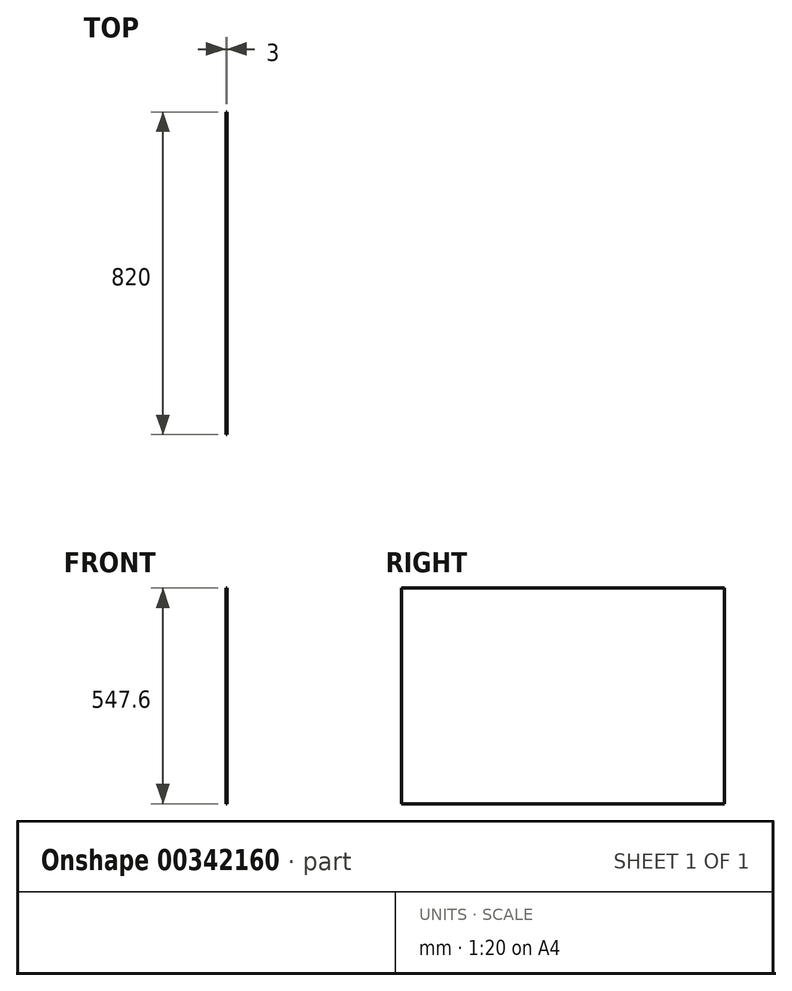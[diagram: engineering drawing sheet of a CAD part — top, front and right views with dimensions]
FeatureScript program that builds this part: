
annotation { "Feature Type Name" : "Feature", "Feature Type Description" : "" }
export const myFeature = defineFeature(function(context is Context, id is Id, definition is map)
    precondition{}
    {
        {
            var Q0;
            Q0=qCreatedBy(makeId("Front.planeOp"),FACE);
            var sketch = newSketch(context, id + "F0", { "sketchPlane" : qUnion([Q0])});
            skLineSegment(sketch, "E0", {"start": v(-856.22, 350.08) * mm, "end": v(-856.22, -197.52) * mm});
            skLineSegment(sketch, "E1", {"start": v(-856.22, -197.52) * mm, "end": v(-291.22, -297.92) * mm});
            skLineSegment(sketch, "E2", {"start": v(1143.78, -552.92) * mm, "end": v(1143.78, -5.32) * mm});
            skLineSegment(sketch, "E3", {"start": v(1143.78, -5.32) * mm, "end": v(-856.22, 350.08) * mm});
            skLineSegment(sketch, "E4.bottom", {"start": v(-856.22, 350.08) * mm, "end": v(-859.22, 350.08) * mm});
            skLineSegment(sketch, "E4.top", {"start": v(-856.22, -197.52) * mm, "end": v(-859.22, -197.52) * mm});
            skLineSegment(sketch, "E4.right", {"start": v(-859.22, 350.08) * mm, "end": v(-859.22, -197.52) * mm});
            skLineSegment(sketch, "E5", {"start": v(-291.22, -297.92) * mm, "end": v(1143.78, -552.92) * mm});
            skLineSegment(sketch, "E6", {"start": v(-291.22, -297.92) * mm, "end": v(-291.22, -552.92) * mm, "construction": true});
            skLineSegment(sketch, "E7", {"start": v(-291.22, -552.92) * mm, "end": v(1143.78, -552.92) * mm, "construction": true});
            skSolve(sketch);
        }
        {
            var Q0;
            Q0=makeQuery(id+"F0.imprint","IMPRINT",FACE,{"disambiguationData":[TD([[makeQuery(id+"F0.imprint","IMPRINT",EDGE,{"derivedFrom":sQuery(id+"F0.wireOp",EDGE,"E4.bottom")}),1.0]])]});
            extrude(context, id + "F1", {"entities" : qUnion([Q0]), "depth" : 820 * mm});
        }
    });
